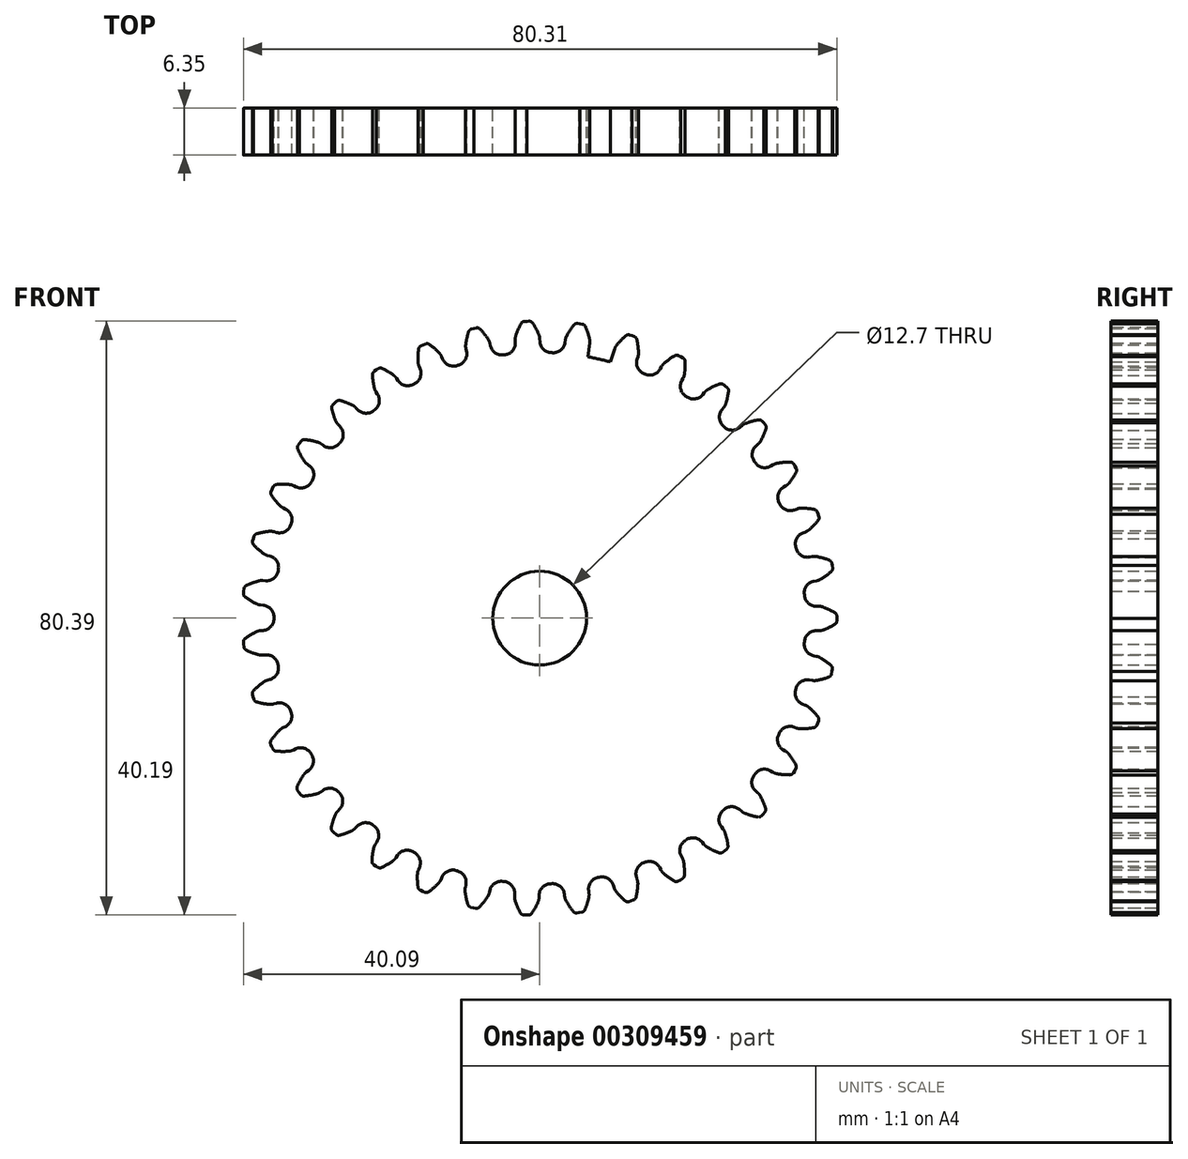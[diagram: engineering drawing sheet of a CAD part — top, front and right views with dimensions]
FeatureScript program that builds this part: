
annotation { "Feature Type Name" : "Feature", "Feature Type Description" : "" }
export const myFeature = defineFeature(function(context is Context, id is Id, definition is map)
    precondition{}
    {
        {
            var Q0;
            Q0=qCreatedBy(makeId("Front.planeOp"),FACE);
            var sketch = newSketch(context, id + "F0", { "sketchPlane" : qUnion([Q0])});
            skCircle(sketch, "E0", {"center": v(0, 0) * mm, "radius": 35.98 * mm});
            skArc(sketch, "E1.trimOffspring", {"start": v(-0.11, 38.38) * mm, "mid": v(-0.5, 39.2) * mm, "end": v(-0.97, 39.97) * mm});
            skLineSegment(sketch, "E2", {"start": v(0.01, 37.83) * mm, "end": v(0.1, 35.98) * mm});
            skLineSegment(sketch, "E3", {"start": v(-1.4, 40.2) * mm, "end": v(-1.75, 40.18) * mm});
            skLineSegment(sketch, "E4.MirrorCS", {"start": v(-2.1, 40.16) * mm, "end": v(-1.75, 40.18) * mm});
            skArc(sketch, "E5.MirrorCS", {"start": v(-3.23, 38.24) * mm, "mid": v(-2.92, 39.09) * mm, "end": v(-2.52, 39.9) * mm});
            skLineSegment(sketch, "E6.MirrorCS", {"start": v(-3.3, 37.68) * mm, "end": v(-3.23, 35.83) * mm});
            skPoint(sketch, "E7.visualSharp", {"position": v(-3.32, 37.96) * mm});
            skArc(sketch, "E7.filletArc", {"start": v(-3.23, 38.24) * mm, "mid": v(-3.3, 37.97) * mm, "end": v(-3.3, 37.68) * mm});
            skPoint(sketch, "E8.visualSharp", {"position": v(0, 38.1) * mm});
            skArc(sketch, "E8.filletArc", {"start": v(0.01, 37.83) * mm, "mid": v(-0.03, 38.1) * mm, "end": v(-0.11, 38.38) * mm});
            skPoint(sketch, "E9.visualSharp", {"position": v(-1.13, 40.2) * mm});
            skArc(sketch, "E9.filletArc", {"start": v(-0.97, 39.97) * mm, "mid": v(-1.16, 40.14) * mm, "end": v(-1.4, 40.2) * mm});
            skPoint(sketch, "E10.visualSharp", {"position": v(-2.38, 40.15) * mm});
            skArc(sketch, "E10.filletArc", {"start": v(-2.1, 40.16) * mm, "mid": v(-2.34, 40.09) * mm, "end": v(-2.52, 39.9) * mm});
            skSolve(sketch);
        }
        {
            var Q0;
            Q0=qCreatedBy(makeId("Front.planeOp"),FACE);
            cPlane(context, id + "F1", {"entities" : qUnion([Q0]), "cplaneType" : CPlaneType.OFFSET, "offset" : 6.35 * mm, "width" : 152.4 * mm, "height" : 152.4 * mm});
        }
        {
            var Q0;
            Q0=qCreatedBy(id+"F1.planeOp",FACE);
            var sketch = newSketch(context, id + "F2", { "sketchPlane" : qUnion([Q0])});
            skArc(sketch, "E11.0.0", {"start": v(-3.23, 35.83) * mm, "mid": v(1.57, -35.94) * mm, "end": v(0.1, 35.98) * mm});
            skArc(sketch, "E11.0.1", {"start": v(0.1, 35.98) * mm, "mid": v(-1.57, 35.94) * mm, "end": v(-3.23, 35.83) * mm});
            skArc(sketch, "E12.0.0", {"start": v(-2.52, 39.9) * mm, "mid": v(-2.92, 39.09) * mm, "end": v(-3.23, 38.24) * mm});
            skArc(sketch, "E12.0.1", {"start": v(-3.23, 38.24) * mm, "mid": v(-3.3, 37.97) * mm, "end": v(-3.3, 37.68) * mm});
            skLineSegment(sketch, "E12.0.2", {"start": v(-3.3, 37.68) * mm, "end": v(-3.23, 35.83) * mm});
            skArc(sketch, "E12.0.3", {"start": v(-3.23, 35.83) * mm, "mid": v(-1.57, 35.94) * mm, "end": v(0.1, 35.98) * mm});
            skLineSegment(sketch, "E12.0.4", {"start": v(0.1, 35.98) * mm, "end": v(0.01, 37.83) * mm});
            skArc(sketch, "E12.0.5", {"start": v(0.01, 37.83) * mm, "mid": v(-0.03, 38.1) * mm, "end": v(-0.11, 38.38) * mm});
            skArc(sketch, "E12.0.6", {"start": v(-0.11, 38.38) * mm, "mid": v(-0.5, 39.2) * mm, "end": v(-0.97, 39.97) * mm});
            skArc(sketch, "E12.0.7", {"start": v(-0.97, 39.97) * mm, "mid": v(-1.16, 40.14) * mm, "end": v(-1.4, 40.2) * mm});
            skLineSegment(sketch, "E12.0.8", {"start": v(-1.4, 40.2) * mm, "end": v(-1.75, 40.18) * mm});
            skLineSegment(sketch, "E12.0.9", {"start": v(-1.75, 40.18) * mm, "end": v(-2.1, 40.16) * mm});
            skArc(sketch, "E12.0.10", {"start": v(-2.1, 40.16) * mm, "mid": v(-2.34, 40.09) * mm, "end": v(-2.52, 39.9) * mm});
            skSolve(sketch);
        }
        {
            var Q0;
            Q0=makeQuery(id+"F2.imprint","IMPRINT",FACE,{"disambiguationData":[TD([[makeQuery(id+"F2.imprint","IMPRINT",EDGE,{"derivedFrom":sQuery(id+"F2.wireOp",EDGE,"E12.0.0")}),1.0]])]});
            var Q1;
            Q1=makeQuery(id+"F0.imprint","IMPRINT",FACE,{"disambiguationData":[TD([[makeQuery(id+"F0.imprint","IMPRINT",EDGE,{"derivedFrom":sQuery(id+"F0.wireOp",EDGE,"E1.trimOffspring")}),1.0]])]});
            loft(context, id + "F3", {"sheetProfilesArray" : [{ "sheetProfileEntities" : qUnion([Q0]) }, { "sheetProfileEntities" : qUnion([Q1]) }]});
        }
        {
            var Q0;
            Q0=qCreatedBy(makeId("Front.planeOp"),FACE);
            var sketch = newSketch(context, id + "F4", { "sketchPlane" : qUnion([Q0])});
            skCircle(sketch, "E13", {"center": v(0, 0) * mm, "radius": 35.98 * mm});
            skSolve(sketch);
        }
        {
            var Q0;
            Q0=makeQuery(id+"F4.imprint","IMPRINT",FACE,{"disambiguationData":[TD([[makeQuery(id+"F4.imprint","IMPRINT",EDGE,{"derivedFrom":sQuery(id+"F4.wireOp",EDGE,"E13")}),1.0]])]});
            var Q1;
            Q1=makeQuery(id+"F3.opLoft","CAP_FACE",FACE,{"disambiguationData":[OSD([makeQuery(id+"F2.imprint","IMPRINT",FACE,{"disambiguationData":[TD([[makeQuery(id+"F2.imprint","IMPRINT",EDGE,{"derivedFrom":sQuery(id+"F2.wireOp",EDGE,"E12.0.0")}),1.0]])]})])],"isStart":true});
            extrude(context, id + "F5", {"entities" : qUnion([Q0]), "endBound" : BoundingType.UP_TO_SURFACE, "endBoundEntityFace" : qUnion([Q1]), "depth" : 25.4 * mm});
        }
        {
            var Q0;
            Q0=makeQuery(id+"F3.opLoft","SWEPT_BODY",BODY,{"disambiguationData":[OSD([makeQuery(id+"F0.imprint","IMPRINT",FACE,{"disambiguationData":[TD([[makeQuery(id+"F0.imprint","IMPRINT",EDGE,{"derivedFrom":sQuery(id+"F0.wireOp",EDGE,"E1.trimOffspring")}),1.0]])]}),makeQuery(id+"F2.imprint","IMPRINT",FACE,{"disambiguationData":[TD([[makeQuery(id+"F2.imprint","IMPRINT",EDGE,{"derivedFrom":sQuery(id+"F2.wireOp",EDGE,"E12.0.0")}),1.0]])]})])]});
            var Q1;
            Q1=makeQuery(id+"F5.opExtrude","SWEPT_FACE",FACE,{"disambiguationData":[OSD([sQuery(id+"F4.wireOp",EDGE,"E13")])]});
            circularPattern(context, id + "F6", {"entities" : qUnion([Q0]), "axis" : qUnion([Q1]), "angle" : 360 * degree, "instanceCount" : 35, "equalSpace" : true});
        }
        {
            var Q0;
            Q0=makeQuery(id+"F6.opPattern","COPY",BODY,{"derivedFrom":makeQuery(id+"F3.opLoft","SWEPT_BODY",BODY,{"disambiguationData":[OSD([makeQuery(id+"F0.imprint","IMPRINT",FACE,{"disambiguationData":[TD([[makeQuery(id+"F0.imprint","IMPRINT",EDGE,{"derivedFrom":sQuery(id+"F0.wireOp",EDGE,"E1.trimOffspring")}),1.0]])]}),makeQuery(id+"F2.imprint","IMPRINT",FACE,{"disambiguationData":[TD([[makeQuery(id+"F2.imprint","IMPRINT",EDGE,{"derivedFrom":sQuery(id+"F2.wireOp",EDGE,"E12.0.0")}),1.0]])]})])]}),"instanceName":"1"});
            var Q1;
            Q1=makeQuery(id+"F5.opExtrude","SWEPT_BODY",BODY,{"disambiguationData":[OSD([sQuery(id+"F4.wireOp",EDGE,"E13")])]});
            var Q2;
            Q2=makeQuery(id+"F3.opLoft","SWEPT_BODY",BODY,{"disambiguationData":[OSD([makeQuery(id+"F0.imprint","IMPRINT",FACE,{"disambiguationData":[TD([[makeQuery(id+"F0.imprint","IMPRINT",EDGE,{"derivedFrom":sQuery(id+"F0.wireOp",EDGE,"E1.trimOffspring")}),1.0]])]}),makeQuery(id+"F2.imprint","IMPRINT",FACE,{"disambiguationData":[TD([[makeQuery(id+"F2.imprint","IMPRINT",EDGE,{"derivedFrom":sQuery(id+"F2.wireOp",EDGE,"E12.0.0")}),1.0]])]})])]});
            var Q3;
            Q3=makeQuery(id+"F6.opPattern","COPY",BODY,{"derivedFrom":makeQuery(id+"F3.opLoft","SWEPT_BODY",BODY,{"disambiguationData":[OSD([makeQuery(id+"F0.imprint","IMPRINT",FACE,{"disambiguationData":[TD([[makeQuery(id+"F0.imprint","IMPRINT",EDGE,{"derivedFrom":sQuery(id+"F0.wireOp",EDGE,"E1.trimOffspring")}),1.0]])]}),makeQuery(id+"F2.imprint","IMPRINT",FACE,{"disambiguationData":[TD([[makeQuery(id+"F2.imprint","IMPRINT",EDGE,{"derivedFrom":sQuery(id+"F2.wireOp",EDGE,"E12.0.0")}),1.0]])]})])]}),"instanceName":"34"});
            var Q4;
            Q4=makeQuery(id+"F6.opPattern","COPY",BODY,{"derivedFrom":makeQuery(id+"F3.opLoft","SWEPT_BODY",BODY,{"disambiguationData":[OSD([makeQuery(id+"F0.imprint","IMPRINT",FACE,{"disambiguationData":[TD([[makeQuery(id+"F0.imprint","IMPRINT",EDGE,{"derivedFrom":sQuery(id+"F0.wireOp",EDGE,"E1.trimOffspring")}),1.0]])]}),makeQuery(id+"F2.imprint","IMPRINT",FACE,{"disambiguationData":[TD([[makeQuery(id+"F2.imprint","IMPRINT",EDGE,{"derivedFrom":sQuery(id+"F2.wireOp",EDGE,"E12.0.0")}),1.0]])]})])]}),"instanceName":"33"});
            var Q5;
            Q5=makeQuery(id+"F6.opPattern","COPY",BODY,{"derivedFrom":makeQuery(id+"F3.opLoft","SWEPT_BODY",BODY,{"disambiguationData":[OSD([makeQuery(id+"F0.imprint","IMPRINT",FACE,{"disambiguationData":[TD([[makeQuery(id+"F0.imprint","IMPRINT",EDGE,{"derivedFrom":sQuery(id+"F0.wireOp",EDGE,"E1.trimOffspring")}),1.0]])]}),makeQuery(id+"F2.imprint","IMPRINT",FACE,{"disambiguationData":[TD([[makeQuery(id+"F2.imprint","IMPRINT",EDGE,{"derivedFrom":sQuery(id+"F2.wireOp",EDGE,"E12.0.0")}),1.0]])]})])]}),"instanceName":"32"});
            var Q6;
            Q6=makeQuery(id+"F6.opPattern","COPY",BODY,{"derivedFrom":makeQuery(id+"F3.opLoft","SWEPT_BODY",BODY,{"disambiguationData":[OSD([makeQuery(id+"F0.imprint","IMPRINT",FACE,{"disambiguationData":[TD([[makeQuery(id+"F0.imprint","IMPRINT",EDGE,{"derivedFrom":sQuery(id+"F0.wireOp",EDGE,"E1.trimOffspring")}),1.0]])]}),makeQuery(id+"F2.imprint","IMPRINT",FACE,{"disambiguationData":[TD([[makeQuery(id+"F2.imprint","IMPRINT",EDGE,{"derivedFrom":sQuery(id+"F2.wireOp",EDGE,"E12.0.0")}),1.0]])]})])]}),"instanceName":"31"});
            var Q7;
            Q7=makeQuery(id+"F6.opPattern","COPY",BODY,{"derivedFrom":makeQuery(id+"F3.opLoft","SWEPT_BODY",BODY,{"disambiguationData":[OSD([makeQuery(id+"F0.imprint","IMPRINT",FACE,{"disambiguationData":[TD([[makeQuery(id+"F0.imprint","IMPRINT",EDGE,{"derivedFrom":sQuery(id+"F0.wireOp",EDGE,"E1.trimOffspring")}),1.0]])]}),makeQuery(id+"F2.imprint","IMPRINT",FACE,{"disambiguationData":[TD([[makeQuery(id+"F2.imprint","IMPRINT",EDGE,{"derivedFrom":sQuery(id+"F2.wireOp",EDGE,"E12.0.0")}),1.0]])]})])]}),"instanceName":"30"});
            var Q8;
            Q8=makeQuery(id+"F6.opPattern","COPY",BODY,{"derivedFrom":makeQuery(id+"F3.opLoft","SWEPT_BODY",BODY,{"disambiguationData":[OSD([makeQuery(id+"F0.imprint","IMPRINT",FACE,{"disambiguationData":[TD([[makeQuery(id+"F0.imprint","IMPRINT",EDGE,{"derivedFrom":sQuery(id+"F0.wireOp",EDGE,"E1.trimOffspring")}),1.0]])]}),makeQuery(id+"F2.imprint","IMPRINT",FACE,{"disambiguationData":[TD([[makeQuery(id+"F2.imprint","IMPRINT",EDGE,{"derivedFrom":sQuery(id+"F2.wireOp",EDGE,"E12.0.0")}),1.0]])]})])]}),"instanceName":"29"});
            var Q9;
            Q9=makeQuery(id+"F6.opPattern","COPY",BODY,{"derivedFrom":makeQuery(id+"F3.opLoft","SWEPT_BODY",BODY,{"disambiguationData":[OSD([makeQuery(id+"F0.imprint","IMPRINT",FACE,{"disambiguationData":[TD([[makeQuery(id+"F0.imprint","IMPRINT",EDGE,{"derivedFrom":sQuery(id+"F0.wireOp",EDGE,"E1.trimOffspring")}),1.0]])]}),makeQuery(id+"F2.imprint","IMPRINT",FACE,{"disambiguationData":[TD([[makeQuery(id+"F2.imprint","IMPRINT",EDGE,{"derivedFrom":sQuery(id+"F2.wireOp",EDGE,"E12.0.0")}),1.0]])]})])]}),"instanceName":"2"});
            var Q10;
            Q10=makeQuery(id+"F6.opPattern","COPY",BODY,{"derivedFrom":makeQuery(id+"F3.opLoft","SWEPT_BODY",BODY,{"disambiguationData":[OSD([makeQuery(id+"F0.imprint","IMPRINT",FACE,{"disambiguationData":[TD([[makeQuery(id+"F0.imprint","IMPRINT",EDGE,{"derivedFrom":sQuery(id+"F0.wireOp",EDGE,"E1.trimOffspring")}),1.0]])]}),makeQuery(id+"F2.imprint","IMPRINT",FACE,{"disambiguationData":[TD([[makeQuery(id+"F2.imprint","IMPRINT",EDGE,{"derivedFrom":sQuery(id+"F2.wireOp",EDGE,"E12.0.0")}),1.0]])]})])]}),"instanceName":"3"});
            var Q11;
            Q11=makeQuery(id+"F6.opPattern","COPY",BODY,{"derivedFrom":makeQuery(id+"F3.opLoft","SWEPT_BODY",BODY,{"disambiguationData":[OSD([makeQuery(id+"F0.imprint","IMPRINT",FACE,{"disambiguationData":[TD([[makeQuery(id+"F0.imprint","IMPRINT",EDGE,{"derivedFrom":sQuery(id+"F0.wireOp",EDGE,"E1.trimOffspring")}),1.0]])]}),makeQuery(id+"F2.imprint","IMPRINT",FACE,{"disambiguationData":[TD([[makeQuery(id+"F2.imprint","IMPRINT",EDGE,{"derivedFrom":sQuery(id+"F2.wireOp",EDGE,"E12.0.0")}),1.0]])]})])]}),"instanceName":"4"});
            var Q12;
            Q12=makeQuery(id+"F6.opPattern","COPY",BODY,{"derivedFrom":makeQuery(id+"F3.opLoft","SWEPT_BODY",BODY,{"disambiguationData":[OSD([makeQuery(id+"F0.imprint","IMPRINT",FACE,{"disambiguationData":[TD([[makeQuery(id+"F0.imprint","IMPRINT",EDGE,{"derivedFrom":sQuery(id+"F0.wireOp",EDGE,"E1.trimOffspring")}),1.0]])]}),makeQuery(id+"F2.imprint","IMPRINT",FACE,{"disambiguationData":[TD([[makeQuery(id+"F2.imprint","IMPRINT",EDGE,{"derivedFrom":sQuery(id+"F2.wireOp",EDGE,"E12.0.0")}),1.0]])]})])]}),"instanceName":"5"});
            var Q13;
            Q13=makeQuery(id+"F6.opPattern","COPY",BODY,{"derivedFrom":makeQuery(id+"F3.opLoft","SWEPT_BODY",BODY,{"disambiguationData":[OSD([makeQuery(id+"F0.imprint","IMPRINT",FACE,{"disambiguationData":[TD([[makeQuery(id+"F0.imprint","IMPRINT",EDGE,{"derivedFrom":sQuery(id+"F0.wireOp",EDGE,"E1.trimOffspring")}),1.0]])]}),makeQuery(id+"F2.imprint","IMPRINT",FACE,{"disambiguationData":[TD([[makeQuery(id+"F2.imprint","IMPRINT",EDGE,{"derivedFrom":sQuery(id+"F2.wireOp",EDGE,"E12.0.0")}),1.0]])]})])]}),"instanceName":"6"});
            var Q14;
            Q14=makeQuery(id+"F6.opPattern","COPY",BODY,{"derivedFrom":makeQuery(id+"F3.opLoft","SWEPT_BODY",BODY,{"disambiguationData":[OSD([makeQuery(id+"F0.imprint","IMPRINT",FACE,{"disambiguationData":[TD([[makeQuery(id+"F0.imprint","IMPRINT",EDGE,{"derivedFrom":sQuery(id+"F0.wireOp",EDGE,"E1.trimOffspring")}),1.0]])]}),makeQuery(id+"F2.imprint","IMPRINT",FACE,{"disambiguationData":[TD([[makeQuery(id+"F2.imprint","IMPRINT",EDGE,{"derivedFrom":sQuery(id+"F2.wireOp",EDGE,"E12.0.0")}),1.0]])]})])]}),"instanceName":"7"});
            var Q15;
            Q15=makeQuery(id+"F6.opPattern","COPY",BODY,{"derivedFrom":makeQuery(id+"F3.opLoft","SWEPT_BODY",BODY,{"disambiguationData":[OSD([makeQuery(id+"F0.imprint","IMPRINT",FACE,{"disambiguationData":[TD([[makeQuery(id+"F0.imprint","IMPRINT",EDGE,{"derivedFrom":sQuery(id+"F0.wireOp",EDGE,"E1.trimOffspring")}),1.0]])]}),makeQuery(id+"F2.imprint","IMPRINT",FACE,{"disambiguationData":[TD([[makeQuery(id+"F2.imprint","IMPRINT",EDGE,{"derivedFrom":sQuery(id+"F2.wireOp",EDGE,"E12.0.0")}),1.0]])]})])]}),"instanceName":"8"});
            var Q16;
            Q16=makeQuery(id+"F6.opPattern","COPY",BODY,{"derivedFrom":makeQuery(id+"F3.opLoft","SWEPT_BODY",BODY,{"disambiguationData":[OSD([makeQuery(id+"F0.imprint","IMPRINT",FACE,{"disambiguationData":[TD([[makeQuery(id+"F0.imprint","IMPRINT",EDGE,{"derivedFrom":sQuery(id+"F0.wireOp",EDGE,"E1.trimOffspring")}),1.0]])]}),makeQuery(id+"F2.imprint","IMPRINT",FACE,{"disambiguationData":[TD([[makeQuery(id+"F2.imprint","IMPRINT",EDGE,{"derivedFrom":sQuery(id+"F2.wireOp",EDGE,"E12.0.0")}),1.0]])]})])]}),"instanceName":"9"});
            var Q17;
            Q17=makeQuery(id+"F6.opPattern","COPY",BODY,{"derivedFrom":makeQuery(id+"F3.opLoft","SWEPT_BODY",BODY,{"disambiguationData":[OSD([makeQuery(id+"F0.imprint","IMPRINT",FACE,{"disambiguationData":[TD([[makeQuery(id+"F0.imprint","IMPRINT",EDGE,{"derivedFrom":sQuery(id+"F0.wireOp",EDGE,"E1.trimOffspring")}),1.0]])]}),makeQuery(id+"F2.imprint","IMPRINT",FACE,{"disambiguationData":[TD([[makeQuery(id+"F2.imprint","IMPRINT",EDGE,{"derivedFrom":sQuery(id+"F2.wireOp",EDGE,"E12.0.0")}),1.0]])]})])]}),"instanceName":"10"});
            var Q18;
            Q18=makeQuery(id+"F6.opPattern","COPY",BODY,{"derivedFrom":makeQuery(id+"F3.opLoft","SWEPT_BODY",BODY,{"disambiguationData":[OSD([makeQuery(id+"F0.imprint","IMPRINT",FACE,{"disambiguationData":[TD([[makeQuery(id+"F0.imprint","IMPRINT",EDGE,{"derivedFrom":sQuery(id+"F0.wireOp",EDGE,"E1.trimOffspring")}),1.0]])]}),makeQuery(id+"F2.imprint","IMPRINT",FACE,{"disambiguationData":[TD([[makeQuery(id+"F2.imprint","IMPRINT",EDGE,{"derivedFrom":sQuery(id+"F2.wireOp",EDGE,"E12.0.0")}),1.0]])]})])]}),"instanceName":"27"});
            var Q19;
            Q19=makeQuery(id+"F6.opPattern","COPY",BODY,{"derivedFrom":makeQuery(id+"F3.opLoft","SWEPT_BODY",BODY,{"disambiguationData":[OSD([makeQuery(id+"F0.imprint","IMPRINT",FACE,{"disambiguationData":[TD([[makeQuery(id+"F0.imprint","IMPRINT",EDGE,{"derivedFrom":sQuery(id+"F0.wireOp",EDGE,"E1.trimOffspring")}),1.0]])]}),makeQuery(id+"F2.imprint","IMPRINT",FACE,{"disambiguationData":[TD([[makeQuery(id+"F2.imprint","IMPRINT",EDGE,{"derivedFrom":sQuery(id+"F2.wireOp",EDGE,"E12.0.0")}),1.0]])]})])]}),"instanceName":"28"});
            var Q20;
            Q20=makeQuery(id+"F6.opPattern","COPY",BODY,{"derivedFrom":makeQuery(id+"F3.opLoft","SWEPT_BODY",BODY,{"disambiguationData":[OSD([makeQuery(id+"F0.imprint","IMPRINT",FACE,{"disambiguationData":[TD([[makeQuery(id+"F0.imprint","IMPRINT",EDGE,{"derivedFrom":sQuery(id+"F0.wireOp",EDGE,"E1.trimOffspring")}),1.0]])]}),makeQuery(id+"F2.imprint","IMPRINT",FACE,{"disambiguationData":[TD([[makeQuery(id+"F2.imprint","IMPRINT",EDGE,{"derivedFrom":sQuery(id+"F2.wireOp",EDGE,"E12.0.0")}),1.0]])]})])]}),"instanceName":"26"});
            var Q21;
            Q21=makeQuery(id+"F6.opPattern","COPY",BODY,{"derivedFrom":makeQuery(id+"F3.opLoft","SWEPT_BODY",BODY,{"disambiguationData":[OSD([makeQuery(id+"F0.imprint","IMPRINT",FACE,{"disambiguationData":[TD([[makeQuery(id+"F0.imprint","IMPRINT",EDGE,{"derivedFrom":sQuery(id+"F0.wireOp",EDGE,"E1.trimOffspring")}),1.0]])]}),makeQuery(id+"F2.imprint","IMPRINT",FACE,{"disambiguationData":[TD([[makeQuery(id+"F2.imprint","IMPRINT",EDGE,{"derivedFrom":sQuery(id+"F2.wireOp",EDGE,"E12.0.0")}),1.0]])]})])]}),"instanceName":"25"});
            var Q22;
            Q22=makeQuery(id+"F6.opPattern","COPY",BODY,{"derivedFrom":makeQuery(id+"F3.opLoft","SWEPT_BODY",BODY,{"disambiguationData":[OSD([makeQuery(id+"F0.imprint","IMPRINT",FACE,{"disambiguationData":[TD([[makeQuery(id+"F0.imprint","IMPRINT",EDGE,{"derivedFrom":sQuery(id+"F0.wireOp",EDGE,"E1.trimOffspring")}),1.0]])]}),makeQuery(id+"F2.imprint","IMPRINT",FACE,{"disambiguationData":[TD([[makeQuery(id+"F2.imprint","IMPRINT",EDGE,{"derivedFrom":sQuery(id+"F2.wireOp",EDGE,"E12.0.0")}),1.0]])]})])]}),"instanceName":"24"});
            var Q23;
            Q23=makeQuery(id+"F6.opPattern","COPY",BODY,{"derivedFrom":makeQuery(id+"F3.opLoft","SWEPT_BODY",BODY,{"disambiguationData":[OSD([makeQuery(id+"F0.imprint","IMPRINT",FACE,{"disambiguationData":[TD([[makeQuery(id+"F0.imprint","IMPRINT",EDGE,{"derivedFrom":sQuery(id+"F0.wireOp",EDGE,"E1.trimOffspring")}),1.0]])]}),makeQuery(id+"F2.imprint","IMPRINT",FACE,{"disambiguationData":[TD([[makeQuery(id+"F2.imprint","IMPRINT",EDGE,{"derivedFrom":sQuery(id+"F2.wireOp",EDGE,"E12.0.0")}),1.0]])]})])]}),"instanceName":"23"});
            var Q24;
            Q24=makeQuery(id+"F6.opPattern","COPY",BODY,{"derivedFrom":makeQuery(id+"F3.opLoft","SWEPT_BODY",BODY,{"disambiguationData":[OSD([makeQuery(id+"F0.imprint","IMPRINT",FACE,{"disambiguationData":[TD([[makeQuery(id+"F0.imprint","IMPRINT",EDGE,{"derivedFrom":sQuery(id+"F0.wireOp",EDGE,"E1.trimOffspring")}),1.0]])]}),makeQuery(id+"F2.imprint","IMPRINT",FACE,{"disambiguationData":[TD([[makeQuery(id+"F2.imprint","IMPRINT",EDGE,{"derivedFrom":sQuery(id+"F2.wireOp",EDGE,"E12.0.0")}),1.0]])]})])]}),"instanceName":"22"});
            var Q25;
            Q25=makeQuery(id+"F6.opPattern","COPY",BODY,{"derivedFrom":makeQuery(id+"F3.opLoft","SWEPT_BODY",BODY,{"disambiguationData":[OSD([makeQuery(id+"F0.imprint","IMPRINT",FACE,{"disambiguationData":[TD([[makeQuery(id+"F0.imprint","IMPRINT",EDGE,{"derivedFrom":sQuery(id+"F0.wireOp",EDGE,"E1.trimOffspring")}),1.0]])]}),makeQuery(id+"F2.imprint","IMPRINT",FACE,{"disambiguationData":[TD([[makeQuery(id+"F2.imprint","IMPRINT",EDGE,{"derivedFrom":sQuery(id+"F2.wireOp",EDGE,"E12.0.0")}),1.0]])]})])]}),"instanceName":"21"});
            var Q26;
            Q26=makeQuery(id+"F6.opPattern","COPY",BODY,{"derivedFrom":makeQuery(id+"F3.opLoft","SWEPT_BODY",BODY,{"disambiguationData":[OSD([makeQuery(id+"F0.imprint","IMPRINT",FACE,{"disambiguationData":[TD([[makeQuery(id+"F0.imprint","IMPRINT",EDGE,{"derivedFrom":sQuery(id+"F0.wireOp",EDGE,"E1.trimOffspring")}),1.0]])]}),makeQuery(id+"F2.imprint","IMPRINT",FACE,{"disambiguationData":[TD([[makeQuery(id+"F2.imprint","IMPRINT",EDGE,{"derivedFrom":sQuery(id+"F2.wireOp",EDGE,"E12.0.0")}),1.0]])]})])]}),"instanceName":"20"});
            var Q27;
            Q27=makeQuery(id+"F6.opPattern","COPY",BODY,{"derivedFrom":makeQuery(id+"F3.opLoft","SWEPT_BODY",BODY,{"disambiguationData":[OSD([makeQuery(id+"F0.imprint","IMPRINT",FACE,{"disambiguationData":[TD([[makeQuery(id+"F0.imprint","IMPRINT",EDGE,{"derivedFrom":sQuery(id+"F0.wireOp",EDGE,"E1.trimOffspring")}),1.0]])]}),makeQuery(id+"F2.imprint","IMPRINT",FACE,{"disambiguationData":[TD([[makeQuery(id+"F2.imprint","IMPRINT",EDGE,{"derivedFrom":sQuery(id+"F2.wireOp",EDGE,"E12.0.0")}),1.0]])]})])]}),"instanceName":"19"});
            var Q28;
            Q28=makeQuery(id+"F6.opPattern","COPY",BODY,{"derivedFrom":makeQuery(id+"F3.opLoft","SWEPT_BODY",BODY,{"disambiguationData":[OSD([makeQuery(id+"F0.imprint","IMPRINT",FACE,{"disambiguationData":[TD([[makeQuery(id+"F0.imprint","IMPRINT",EDGE,{"derivedFrom":sQuery(id+"F0.wireOp",EDGE,"E1.trimOffspring")}),1.0]])]}),makeQuery(id+"F2.imprint","IMPRINT",FACE,{"disambiguationData":[TD([[makeQuery(id+"F2.imprint","IMPRINT",EDGE,{"derivedFrom":sQuery(id+"F2.wireOp",EDGE,"E12.0.0")}),1.0]])]})])]}),"instanceName":"18"});
            var Q29;
            Q29=makeQuery(id+"F6.opPattern","COPY",BODY,{"derivedFrom":makeQuery(id+"F3.opLoft","SWEPT_BODY",BODY,{"disambiguationData":[OSD([makeQuery(id+"F0.imprint","IMPRINT",FACE,{"disambiguationData":[TD([[makeQuery(id+"F0.imprint","IMPRINT",EDGE,{"derivedFrom":sQuery(id+"F0.wireOp",EDGE,"E1.trimOffspring")}),1.0]])]}),makeQuery(id+"F2.imprint","IMPRINT",FACE,{"disambiguationData":[TD([[makeQuery(id+"F2.imprint","IMPRINT",EDGE,{"derivedFrom":sQuery(id+"F2.wireOp",EDGE,"E12.0.0")}),1.0]])]})])]}),"instanceName":"17"});
            var Q30;
            Q30=makeQuery(id+"F6.opPattern","COPY",BODY,{"derivedFrom":makeQuery(id+"F3.opLoft","SWEPT_BODY",BODY,{"disambiguationData":[OSD([makeQuery(id+"F0.imprint","IMPRINT",FACE,{"disambiguationData":[TD([[makeQuery(id+"F0.imprint","IMPRINT",EDGE,{"derivedFrom":sQuery(id+"F0.wireOp",EDGE,"E1.trimOffspring")}),1.0]])]}),makeQuery(id+"F2.imprint","IMPRINT",FACE,{"disambiguationData":[TD([[makeQuery(id+"F2.imprint","IMPRINT",EDGE,{"derivedFrom":sQuery(id+"F2.wireOp",EDGE,"E12.0.0")}),1.0]])]})])]}),"instanceName":"16"});
            var Q31;
            Q31=makeQuery(id+"F6.opPattern","COPY",BODY,{"derivedFrom":makeQuery(id+"F3.opLoft","SWEPT_BODY",BODY,{"disambiguationData":[OSD([makeQuery(id+"F0.imprint","IMPRINT",FACE,{"disambiguationData":[TD([[makeQuery(id+"F0.imprint","IMPRINT",EDGE,{"derivedFrom":sQuery(id+"F0.wireOp",EDGE,"E1.trimOffspring")}),1.0]])]}),makeQuery(id+"F2.imprint","IMPRINT",FACE,{"disambiguationData":[TD([[makeQuery(id+"F2.imprint","IMPRINT",EDGE,{"derivedFrom":sQuery(id+"F2.wireOp",EDGE,"E12.0.0")}),1.0]])]})])]}),"instanceName":"15"});
            var Q32;
            Q32=makeQuery(id+"F6.opPattern","COPY",BODY,{"derivedFrom":makeQuery(id+"F3.opLoft","SWEPT_BODY",BODY,{"disambiguationData":[OSD([makeQuery(id+"F0.imprint","IMPRINT",FACE,{"disambiguationData":[TD([[makeQuery(id+"F0.imprint","IMPRINT",EDGE,{"derivedFrom":sQuery(id+"F0.wireOp",EDGE,"E1.trimOffspring")}),1.0]])]}),makeQuery(id+"F2.imprint","IMPRINT",FACE,{"disambiguationData":[TD([[makeQuery(id+"F2.imprint","IMPRINT",EDGE,{"derivedFrom":sQuery(id+"F2.wireOp",EDGE,"E12.0.0")}),1.0]])]})])]}),"instanceName":"14"});
            var Q33;
            Q33=makeQuery(id+"F6.opPattern","COPY",BODY,{"derivedFrom":makeQuery(id+"F3.opLoft","SWEPT_BODY",BODY,{"disambiguationData":[OSD([makeQuery(id+"F0.imprint","IMPRINT",FACE,{"disambiguationData":[TD([[makeQuery(id+"F0.imprint","IMPRINT",EDGE,{"derivedFrom":sQuery(id+"F0.wireOp",EDGE,"E1.trimOffspring")}),1.0]])]}),makeQuery(id+"F2.imprint","IMPRINT",FACE,{"disambiguationData":[TD([[makeQuery(id+"F2.imprint","IMPRINT",EDGE,{"derivedFrom":sQuery(id+"F2.wireOp",EDGE,"E12.0.0")}),1.0]])]})])]}),"instanceName":"13"});
            var Q34;
            Q34=makeQuery(id+"F6.opPattern","COPY",BODY,{"derivedFrom":makeQuery(id+"F3.opLoft","SWEPT_BODY",BODY,{"disambiguationData":[OSD([makeQuery(id+"F0.imprint","IMPRINT",FACE,{"disambiguationData":[TD([[makeQuery(id+"F0.imprint","IMPRINT",EDGE,{"derivedFrom":sQuery(id+"F0.wireOp",EDGE,"E1.trimOffspring")}),1.0]])]}),makeQuery(id+"F2.imprint","IMPRINT",FACE,{"disambiguationData":[TD([[makeQuery(id+"F2.imprint","IMPRINT",EDGE,{"derivedFrom":sQuery(id+"F2.wireOp",EDGE,"E12.0.0")}),1.0]])]})])]}),"instanceName":"12"});
            var Q35;
            Q35=makeQuery(id+"F6.opPattern","COPY",BODY,{"derivedFrom":makeQuery(id+"F3.opLoft","SWEPT_BODY",BODY,{"disambiguationData":[OSD([makeQuery(id+"F0.imprint","IMPRINT",FACE,{"disambiguationData":[TD([[makeQuery(id+"F0.imprint","IMPRINT",EDGE,{"derivedFrom":sQuery(id+"F0.wireOp",EDGE,"E1.trimOffspring")}),1.0]])]}),makeQuery(id+"F2.imprint","IMPRINT",FACE,{"disambiguationData":[TD([[makeQuery(id+"F2.imprint","IMPRINT",EDGE,{"derivedFrom":sQuery(id+"F2.wireOp",EDGE,"E12.0.0")}),1.0]])]})])]}),"instanceName":"11"});
            booleanBodies(context, id + "F7", {"operationType" : BooleanOperationType.UNION, "tools" : qUnion([Q0, Q1, Q2, Q3, Q4, Q5, Q6, Q7, Q8, Q9, Q10, Q11, Q12, Q13, Q14, Q15, Q16, Q17, Q18, Q19, Q20, Q21, Q22, Q23, Q24, Q25, Q26, Q27, Q28, Q29, Q30, Q31, Q32, Q33, Q34, Q35])});
        }
        {
            var Q0;
            Q0=makeQuery(id+"F3.opLoft","SWEPT_EDGE",EDGE,{"disambiguationData":[OSD([sQuery(id+"F0.wireOp",EDGE,"E0"),sQuery(id+"F0.wireOp",EDGE,"E2"),sQuery(id+"F2.wireOp",EDGE,"E11.0.0"),sQuery(id+"F2.wireOp",EDGE,"E12.0.3"),sQuery(id+"F2.wireOp",EDGE,"E12.0.4")])]});
            var Q1;
            Q1=makeQuery(id+"F6.opPattern","COPY",EDGE,{"derivedFrom":makeQuery(id+"F3.opLoft","SWEPT_EDGE",EDGE,{"disambiguationData":[OSD([sQuery(id+"F0.wireOp",EDGE,"E0"),sQuery(id+"F0.wireOp",EDGE,"E2"),sQuery(id+"F2.wireOp",EDGE,"E11.0.0"),sQuery(id+"F2.wireOp",EDGE,"E12.0.3"),sQuery(id+"F2.wireOp",EDGE,"E12.0.4")])]}),"instanceName":"34"});
            var Q2;
            Q2=makeQuery(id+"F6.opPattern","COPY",EDGE,{"derivedFrom":makeQuery(id+"F3.opLoft","SWEPT_EDGE",EDGE,{"disambiguationData":[OSD([sQuery(id+"F0.wireOp",EDGE,"E0"),sQuery(id+"F0.wireOp",EDGE,"E2"),sQuery(id+"F2.wireOp",EDGE,"E11.0.0"),sQuery(id+"F2.wireOp",EDGE,"E12.0.3"),sQuery(id+"F2.wireOp",EDGE,"E12.0.4")])]}),"instanceName":"33"});
            var Q3;
            Q3=makeQuery(id+"F6.opPattern","COPY",EDGE,{"derivedFrom":makeQuery(id+"F3.opLoft","SWEPT_EDGE",EDGE,{"disambiguationData":[OSD([sQuery(id+"F0.wireOp",EDGE,"E0"),sQuery(id+"F0.wireOp",EDGE,"E2"),sQuery(id+"F2.wireOp",EDGE,"E11.0.0"),sQuery(id+"F2.wireOp",EDGE,"E12.0.3"),sQuery(id+"F2.wireOp",EDGE,"E12.0.4")])]}),"instanceName":"32"});
            var Q4;
            Q4=makeQuery(id+"F6.opPattern","COPY",EDGE,{"derivedFrom":makeQuery(id+"F3.opLoft","SWEPT_EDGE",EDGE,{"disambiguationData":[OSD([sQuery(id+"F0.wireOp",EDGE,"E0"),sQuery(id+"F0.wireOp",EDGE,"E2"),sQuery(id+"F2.wireOp",EDGE,"E11.0.0"),sQuery(id+"F2.wireOp",EDGE,"E12.0.3"),sQuery(id+"F2.wireOp",EDGE,"E12.0.4")])]}),"instanceName":"31"});
            var Q5;
            Q5=makeQuery(id+"F3.opLoft","SWEPT_EDGE",EDGE,{"disambiguationData":[OSD([sQuery(id+"F0.wireOp",EDGE,"E0"),sQuery(id+"F0.wireOp",EDGE,"E6.MirrorCS"),sQuery(id+"F2.wireOp",EDGE,"E11.0.0"),sQuery(id+"F2.wireOp",EDGE,"E12.0.2"),sQuery(id+"F2.wireOp",EDGE,"E12.0.3")])]});
            var Q6;
            Q6=makeQuery(id+"F6.opPattern","COPY",EDGE,{"derivedFrom":makeQuery(id+"F3.opLoft","SWEPT_EDGE",EDGE,{"disambiguationData":[OSD([sQuery(id+"F0.wireOp",EDGE,"E0"),sQuery(id+"F0.wireOp",EDGE,"E6.MirrorCS"),sQuery(id+"F2.wireOp",EDGE,"E11.0.0"),sQuery(id+"F2.wireOp",EDGE,"E12.0.2"),sQuery(id+"F2.wireOp",EDGE,"E12.0.3")])]}),"instanceName":"33"});
            var Q7;
            Q7=makeQuery(id+"F6.opPattern","COPY",EDGE,{"derivedFrom":makeQuery(id+"F3.opLoft","SWEPT_EDGE",EDGE,{"disambiguationData":[OSD([sQuery(id+"F0.wireOp",EDGE,"E0"),sQuery(id+"F0.wireOp",EDGE,"E6.MirrorCS"),sQuery(id+"F2.wireOp",EDGE,"E11.0.0"),sQuery(id+"F2.wireOp",EDGE,"E12.0.2"),sQuery(id+"F2.wireOp",EDGE,"E12.0.3")])]}),"instanceName":"34"});
            var Q8;
            Q8=makeQuery(id+"F6.opPattern","COPY",EDGE,{"derivedFrom":makeQuery(id+"F3.opLoft","SWEPT_EDGE",EDGE,{"disambiguationData":[OSD([sQuery(id+"F0.wireOp",EDGE,"E0"),sQuery(id+"F0.wireOp",EDGE,"E6.MirrorCS"),sQuery(id+"F2.wireOp",EDGE,"E11.0.0"),sQuery(id+"F2.wireOp",EDGE,"E12.0.2"),sQuery(id+"F2.wireOp",EDGE,"E12.0.3")])]}),"instanceName":"32"});
            var Q9;
            Q9=makeQuery(id+"F6.opPattern","COPY",EDGE,{"derivedFrom":makeQuery(id+"F3.opLoft","SWEPT_EDGE",EDGE,{"disambiguationData":[OSD([sQuery(id+"F0.wireOp",EDGE,"E0"),sQuery(id+"F0.wireOp",EDGE,"E2"),sQuery(id+"F2.wireOp",EDGE,"E11.0.0"),sQuery(id+"F2.wireOp",EDGE,"E12.0.3"),sQuery(id+"F2.wireOp",EDGE,"E12.0.4")])]}),"instanceName":"30"});
            var Q10;
            Q10=makeQuery(id+"F6.opPattern","COPY",EDGE,{"derivedFrom":makeQuery(id+"F3.opLoft","SWEPT_EDGE",EDGE,{"disambiguationData":[OSD([sQuery(id+"F0.wireOp",EDGE,"E0"),sQuery(id+"F0.wireOp",EDGE,"E6.MirrorCS"),sQuery(id+"F2.wireOp",EDGE,"E11.0.0"),sQuery(id+"F2.wireOp",EDGE,"E12.0.2"),sQuery(id+"F2.wireOp",EDGE,"E12.0.3")])]}),"instanceName":"31"});
            var Q11;
            Q11=makeQuery(id+"F6.opPattern","COPY",EDGE,{"derivedFrom":makeQuery(id+"F3.opLoft","SWEPT_EDGE",EDGE,{"disambiguationData":[OSD([sQuery(id+"F0.wireOp",EDGE,"E0"),sQuery(id+"F0.wireOp",EDGE,"E6.MirrorCS"),sQuery(id+"F2.wireOp",EDGE,"E11.0.0"),sQuery(id+"F2.wireOp",EDGE,"E12.0.2"),sQuery(id+"F2.wireOp",EDGE,"E12.0.3")])]}),"instanceName":"30"});
            var Q12;
            Q12=makeQuery(id+"F6.opPattern","COPY",EDGE,{"derivedFrom":makeQuery(id+"F3.opLoft","SWEPT_EDGE",EDGE,{"disambiguationData":[OSD([sQuery(id+"F0.wireOp",EDGE,"E0"),sQuery(id+"F0.wireOp",EDGE,"E2"),sQuery(id+"F2.wireOp",EDGE,"E11.0.0"),sQuery(id+"F2.wireOp",EDGE,"E12.0.3"),sQuery(id+"F2.wireOp",EDGE,"E12.0.4")])]}),"instanceName":"29"});
            var Q13;
            Q13=makeQuery(id+"F6.opPattern","COPY",EDGE,{"derivedFrom":makeQuery(id+"F3.opLoft","SWEPT_EDGE",EDGE,{"disambiguationData":[OSD([sQuery(id+"F0.wireOp",EDGE,"E0"),sQuery(id+"F0.wireOp",EDGE,"E6.MirrorCS"),sQuery(id+"F2.wireOp",EDGE,"E11.0.0"),sQuery(id+"F2.wireOp",EDGE,"E12.0.2"),sQuery(id+"F2.wireOp",EDGE,"E12.0.3")])]}),"instanceName":"1"});
            var Q14;
            Q14=makeQuery(id+"F6.opPattern","COPY",EDGE,{"derivedFrom":makeQuery(id+"F3.opLoft","SWEPT_EDGE",EDGE,{"disambiguationData":[OSD([sQuery(id+"F0.wireOp",EDGE,"E0"),sQuery(id+"F0.wireOp",EDGE,"E6.MirrorCS"),sQuery(id+"F2.wireOp",EDGE,"E11.0.0"),sQuery(id+"F2.wireOp",EDGE,"E12.0.2"),sQuery(id+"F2.wireOp",EDGE,"E12.0.3")])]}),"instanceName":"2"});
            var Q15;
            Q15=makeQuery(id+"F6.opPattern","COPY",EDGE,{"derivedFrom":makeQuery(id+"F3.opLoft","SWEPT_EDGE",EDGE,{"disambiguationData":[OSD([sQuery(id+"F0.wireOp",EDGE,"E0"),sQuery(id+"F0.wireOp",EDGE,"E6.MirrorCS"),sQuery(id+"F2.wireOp",EDGE,"E11.0.0"),sQuery(id+"F2.wireOp",EDGE,"E12.0.2"),sQuery(id+"F2.wireOp",EDGE,"E12.0.3")])]}),"instanceName":"3"});
            var Q16;
            Q16=makeQuery(id+"F6.opPattern","COPY",EDGE,{"derivedFrom":makeQuery(id+"F3.opLoft","SWEPT_EDGE",EDGE,{"disambiguationData":[OSD([sQuery(id+"F0.wireOp",EDGE,"E0"),sQuery(id+"F0.wireOp",EDGE,"E6.MirrorCS"),sQuery(id+"F2.wireOp",EDGE,"E11.0.0"),sQuery(id+"F2.wireOp",EDGE,"E12.0.2"),sQuery(id+"F2.wireOp",EDGE,"E12.0.3")])]}),"instanceName":"4"});
            var Q17;
            Q17=makeQuery(id+"F6.opPattern","COPY",EDGE,{"derivedFrom":makeQuery(id+"F3.opLoft","SWEPT_EDGE",EDGE,{"disambiguationData":[OSD([sQuery(id+"F0.wireOp",EDGE,"E0"),sQuery(id+"F0.wireOp",EDGE,"E6.MirrorCS"),sQuery(id+"F2.wireOp",EDGE,"E11.0.0"),sQuery(id+"F2.wireOp",EDGE,"E12.0.2"),sQuery(id+"F2.wireOp",EDGE,"E12.0.3")])]}),"instanceName":"5"});
            var Q18;
            Q18=makeQuery(id+"F6.opPattern","COPY",EDGE,{"derivedFrom":makeQuery(id+"F3.opLoft","SWEPT_EDGE",EDGE,{"disambiguationData":[OSD([sQuery(id+"F0.wireOp",EDGE,"E0"),sQuery(id+"F0.wireOp",EDGE,"E6.MirrorCS"),sQuery(id+"F2.wireOp",EDGE,"E11.0.0"),sQuery(id+"F2.wireOp",EDGE,"E12.0.2"),sQuery(id+"F2.wireOp",EDGE,"E12.0.3")])]}),"instanceName":"6"});
            var Q19;
            Q19=makeQuery(id+"F6.opPattern","COPY",EDGE,{"derivedFrom":makeQuery(id+"F3.opLoft","SWEPT_EDGE",EDGE,{"disambiguationData":[OSD([sQuery(id+"F0.wireOp",EDGE,"E0"),sQuery(id+"F0.wireOp",EDGE,"E6.MirrorCS"),sQuery(id+"F2.wireOp",EDGE,"E11.0.0"),sQuery(id+"F2.wireOp",EDGE,"E12.0.2"),sQuery(id+"F2.wireOp",EDGE,"E12.0.3")])]}),"instanceName":"7"});
            var Q20;
            Q20=makeQuery(id+"F6.opPattern","COPY",EDGE,{"derivedFrom":makeQuery(id+"F3.opLoft","SWEPT_EDGE",EDGE,{"disambiguationData":[OSD([sQuery(id+"F0.wireOp",EDGE,"E0"),sQuery(id+"F0.wireOp",EDGE,"E2"),sQuery(id+"F2.wireOp",EDGE,"E11.0.0"),sQuery(id+"F2.wireOp",EDGE,"E12.0.3"),sQuery(id+"F2.wireOp",EDGE,"E12.0.4")])]}),"instanceName":"28"});
            var Q21;
            Q21=makeQuery(id+"F6.opPattern","COPY",EDGE,{"derivedFrom":makeQuery(id+"F3.opLoft","SWEPT_EDGE",EDGE,{"disambiguationData":[OSD([sQuery(id+"F0.wireOp",EDGE,"E0"),sQuery(id+"F0.wireOp",EDGE,"E2"),sQuery(id+"F2.wireOp",EDGE,"E11.0.0"),sQuery(id+"F2.wireOp",EDGE,"E12.0.3"),sQuery(id+"F2.wireOp",EDGE,"E12.0.4")])]}),"instanceName":"27"});
            var Q22;
            Q22=makeQuery(id+"F6.opPattern","COPY",EDGE,{"derivedFrom":makeQuery(id+"F3.opLoft","SWEPT_EDGE",EDGE,{"disambiguationData":[OSD([sQuery(id+"F0.wireOp",EDGE,"E0"),sQuery(id+"F0.wireOp",EDGE,"E2"),sQuery(id+"F2.wireOp",EDGE,"E11.0.0"),sQuery(id+"F2.wireOp",EDGE,"E12.0.3"),sQuery(id+"F2.wireOp",EDGE,"E12.0.4")])]}),"instanceName":"26"});
            var Q23;
            Q23=makeQuery(id+"F6.opPattern","COPY",EDGE,{"derivedFrom":makeQuery(id+"F3.opLoft","SWEPT_EDGE",EDGE,{"disambiguationData":[OSD([sQuery(id+"F0.wireOp",EDGE,"E0"),sQuery(id+"F0.wireOp",EDGE,"E2"),sQuery(id+"F2.wireOp",EDGE,"E11.0.0"),sQuery(id+"F2.wireOp",EDGE,"E12.0.3"),sQuery(id+"F2.wireOp",EDGE,"E12.0.4")])]}),"instanceName":"25"});
            var Q24;
            Q24=makeQuery(id+"F6.opPattern","COPY",EDGE,{"derivedFrom":makeQuery(id+"F3.opLoft","SWEPT_EDGE",EDGE,{"disambiguationData":[OSD([sQuery(id+"F0.wireOp",EDGE,"E0"),sQuery(id+"F0.wireOp",EDGE,"E2"),sQuery(id+"F2.wireOp",EDGE,"E11.0.0"),sQuery(id+"F2.wireOp",EDGE,"E12.0.3"),sQuery(id+"F2.wireOp",EDGE,"E12.0.4")])]}),"instanceName":"24"});
            var Q25;
            Q25=makeQuery(id+"F6.opPattern","COPY",EDGE,{"derivedFrom":makeQuery(id+"F3.opLoft","SWEPT_EDGE",EDGE,{"disambiguationData":[OSD([sQuery(id+"F0.wireOp",EDGE,"E0"),sQuery(id+"F0.wireOp",EDGE,"E2"),sQuery(id+"F2.wireOp",EDGE,"E11.0.0"),sQuery(id+"F2.wireOp",EDGE,"E12.0.3"),sQuery(id+"F2.wireOp",EDGE,"E12.0.4")])]}),"instanceName":"23"});
            var Q26;
            Q26=makeQuery(id+"F6.opPattern","COPY",EDGE,{"derivedFrom":makeQuery(id+"F3.opLoft","SWEPT_EDGE",EDGE,{"disambiguationData":[OSD([sQuery(id+"F0.wireOp",EDGE,"E0"),sQuery(id+"F0.wireOp",EDGE,"E2"),sQuery(id+"F2.wireOp",EDGE,"E11.0.0"),sQuery(id+"F2.wireOp",EDGE,"E12.0.3"),sQuery(id+"F2.wireOp",EDGE,"E12.0.4")])]}),"instanceName":"22"});
            var Q27;
            Q27=makeQuery(id+"F6.opPattern","COPY",EDGE,{"derivedFrom":makeQuery(id+"F3.opLoft","SWEPT_EDGE",EDGE,{"disambiguationData":[OSD([sQuery(id+"F0.wireOp",EDGE,"E0"),sQuery(id+"F0.wireOp",EDGE,"E2"),sQuery(id+"F2.wireOp",EDGE,"E11.0.0"),sQuery(id+"F2.wireOp",EDGE,"E12.0.3"),sQuery(id+"F2.wireOp",EDGE,"E12.0.4")])]}),"instanceName":"21"});
            var Q28;
            Q28=makeQuery(id+"F6.opPattern","COPY",EDGE,{"derivedFrom":makeQuery(id+"F3.opLoft","SWEPT_EDGE",EDGE,{"disambiguationData":[OSD([sQuery(id+"F0.wireOp",EDGE,"E0"),sQuery(id+"F0.wireOp",EDGE,"E2"),sQuery(id+"F2.wireOp",EDGE,"E11.0.0"),sQuery(id+"F2.wireOp",EDGE,"E12.0.3"),sQuery(id+"F2.wireOp",EDGE,"E12.0.4")])]}),"instanceName":"20"});
            var Q29;
            Q29=makeQuery(id+"F6.opPattern","COPY",EDGE,{"derivedFrom":makeQuery(id+"F3.opLoft","SWEPT_EDGE",EDGE,{"disambiguationData":[OSD([sQuery(id+"F0.wireOp",EDGE,"E0"),sQuery(id+"F0.wireOp",EDGE,"E2"),sQuery(id+"F2.wireOp",EDGE,"E11.0.0"),sQuery(id+"F2.wireOp",EDGE,"E12.0.3"),sQuery(id+"F2.wireOp",EDGE,"E12.0.4")])]}),"instanceName":"19"});
            var Q30;
            Q30=makeQuery(id+"F6.opPattern","COPY",EDGE,{"derivedFrom":makeQuery(id+"F3.opLoft","SWEPT_EDGE",EDGE,{"disambiguationData":[OSD([sQuery(id+"F0.wireOp",EDGE,"E0"),sQuery(id+"F0.wireOp",EDGE,"E2"),sQuery(id+"F2.wireOp",EDGE,"E11.0.0"),sQuery(id+"F2.wireOp",EDGE,"E12.0.3"),sQuery(id+"F2.wireOp",EDGE,"E12.0.4")])]}),"instanceName":"18"});
            var Q31;
            Q31=makeQuery(id+"F6.opPattern","COPY",EDGE,{"derivedFrom":makeQuery(id+"F3.opLoft","SWEPT_EDGE",EDGE,{"disambiguationData":[OSD([sQuery(id+"F0.wireOp",EDGE,"E0"),sQuery(id+"F0.wireOp",EDGE,"E2"),sQuery(id+"F2.wireOp",EDGE,"E11.0.0"),sQuery(id+"F2.wireOp",EDGE,"E12.0.3"),sQuery(id+"F2.wireOp",EDGE,"E12.0.4")])]}),"instanceName":"17"});
            var Q32;
            Q32=makeQuery(id+"F6.opPattern","COPY",EDGE,{"derivedFrom":makeQuery(id+"F3.opLoft","SWEPT_EDGE",EDGE,{"disambiguationData":[OSD([sQuery(id+"F0.wireOp",EDGE,"E0"),sQuery(id+"F0.wireOp",EDGE,"E2"),sQuery(id+"F2.wireOp",EDGE,"E11.0.0"),sQuery(id+"F2.wireOp",EDGE,"E12.0.3"),sQuery(id+"F2.wireOp",EDGE,"E12.0.4")])]}),"instanceName":"16"});
            var Q33;
            Q33=makeQuery(id+"F6.opPattern","COPY",EDGE,{"derivedFrom":makeQuery(id+"F3.opLoft","SWEPT_EDGE",EDGE,{"disambiguationData":[OSD([sQuery(id+"F0.wireOp",EDGE,"E0"),sQuery(id+"F0.wireOp",EDGE,"E2"),sQuery(id+"F2.wireOp",EDGE,"E11.0.0"),sQuery(id+"F2.wireOp",EDGE,"E12.0.3"),sQuery(id+"F2.wireOp",EDGE,"E12.0.4")])]}),"instanceName":"7"});
            var Q34;
            Q34=makeQuery(id+"F6.opPattern","COPY",EDGE,{"derivedFrom":makeQuery(id+"F3.opLoft","SWEPT_EDGE",EDGE,{"disambiguationData":[OSD([sQuery(id+"F0.wireOp",EDGE,"E0"),sQuery(id+"F0.wireOp",EDGE,"E2"),sQuery(id+"F2.wireOp",EDGE,"E11.0.0"),sQuery(id+"F2.wireOp",EDGE,"E12.0.3"),sQuery(id+"F2.wireOp",EDGE,"E12.0.4")])]}),"instanceName":"8"});
            var Q35;
            Q35=makeQuery(id+"F6.opPattern","COPY",EDGE,{"derivedFrom":makeQuery(id+"F3.opLoft","SWEPT_EDGE",EDGE,{"disambiguationData":[OSD([sQuery(id+"F0.wireOp",EDGE,"E0"),sQuery(id+"F0.wireOp",EDGE,"E2"),sQuery(id+"F2.wireOp",EDGE,"E11.0.0"),sQuery(id+"F2.wireOp",EDGE,"E12.0.3"),sQuery(id+"F2.wireOp",EDGE,"E12.0.4")])]}),"instanceName":"9"});
            var Q36;
            Q36=makeQuery(id+"F6.opPattern","COPY",EDGE,{"derivedFrom":makeQuery(id+"F3.opLoft","SWEPT_EDGE",EDGE,{"disambiguationData":[OSD([sQuery(id+"F0.wireOp",EDGE,"E0"),sQuery(id+"F0.wireOp",EDGE,"E2"),sQuery(id+"F2.wireOp",EDGE,"E11.0.0"),sQuery(id+"F2.wireOp",EDGE,"E12.0.3"),sQuery(id+"F2.wireOp",EDGE,"E12.0.4")])]}),"instanceName":"10"});
            var Q37;
            Q37=makeQuery(id+"F6.opPattern","COPY",EDGE,{"derivedFrom":makeQuery(id+"F3.opLoft","SWEPT_EDGE",EDGE,{"disambiguationData":[OSD([sQuery(id+"F0.wireOp",EDGE,"E0"),sQuery(id+"F0.wireOp",EDGE,"E2"),sQuery(id+"F2.wireOp",EDGE,"E11.0.0"),sQuery(id+"F2.wireOp",EDGE,"E12.0.3"),sQuery(id+"F2.wireOp",EDGE,"E12.0.4")])]}),"instanceName":"11"});
            var Q38;
            Q38=makeQuery(id+"F6.opPattern","COPY",EDGE,{"derivedFrom":makeQuery(id+"F3.opLoft","SWEPT_EDGE",EDGE,{"disambiguationData":[OSD([sQuery(id+"F0.wireOp",EDGE,"E0"),sQuery(id+"F0.wireOp",EDGE,"E2"),sQuery(id+"F2.wireOp",EDGE,"E11.0.0"),sQuery(id+"F2.wireOp",EDGE,"E12.0.3"),sQuery(id+"F2.wireOp",EDGE,"E12.0.4")])]}),"instanceName":"12"});
            var Q39;
            Q39=makeQuery(id+"F6.opPattern","COPY",EDGE,{"derivedFrom":makeQuery(id+"F3.opLoft","SWEPT_EDGE",EDGE,{"disambiguationData":[OSD([sQuery(id+"F0.wireOp",EDGE,"E0"),sQuery(id+"F0.wireOp",EDGE,"E2"),sQuery(id+"F2.wireOp",EDGE,"E11.0.0"),sQuery(id+"F2.wireOp",EDGE,"E12.0.3"),sQuery(id+"F2.wireOp",EDGE,"E12.0.4")])]}),"instanceName":"13"});
            var Q40;
            Q40=makeQuery(id+"F6.opPattern","COPY",EDGE,{"derivedFrom":makeQuery(id+"F3.opLoft","SWEPT_EDGE",EDGE,{"disambiguationData":[OSD([sQuery(id+"F0.wireOp",EDGE,"E0"),sQuery(id+"F0.wireOp",EDGE,"E2"),sQuery(id+"F2.wireOp",EDGE,"E11.0.0"),sQuery(id+"F2.wireOp",EDGE,"E12.0.3"),sQuery(id+"F2.wireOp",EDGE,"E12.0.4")])]}),"instanceName":"14"});
            var Q41;
            Q41=makeQuery(id+"F6.opPattern","COPY",EDGE,{"derivedFrom":makeQuery(id+"F3.opLoft","SWEPT_EDGE",EDGE,{"disambiguationData":[OSD([sQuery(id+"F0.wireOp",EDGE,"E0"),sQuery(id+"F0.wireOp",EDGE,"E2"),sQuery(id+"F2.wireOp",EDGE,"E11.0.0"),sQuery(id+"F2.wireOp",EDGE,"E12.0.3"),sQuery(id+"F2.wireOp",EDGE,"E12.0.4")])]}),"instanceName":"15"});
            var Q42;
            Q42=makeQuery(id+"F6.opPattern","COPY",EDGE,{"derivedFrom":makeQuery(id+"F3.opLoft","SWEPT_EDGE",EDGE,{"disambiguationData":[OSD([sQuery(id+"F0.wireOp",EDGE,"E0"),sQuery(id+"F0.wireOp",EDGE,"E6.MirrorCS"),sQuery(id+"F2.wireOp",EDGE,"E11.0.0"),sQuery(id+"F2.wireOp",EDGE,"E12.0.2"),sQuery(id+"F2.wireOp",EDGE,"E12.0.3")])]}),"instanceName":"18"});
            var Q43;
            Q43=makeQuery(id+"F6.opPattern","COPY",EDGE,{"derivedFrom":makeQuery(id+"F3.opLoft","SWEPT_EDGE",EDGE,{"disambiguationData":[OSD([sQuery(id+"F0.wireOp",EDGE,"E0"),sQuery(id+"F0.wireOp",EDGE,"E6.MirrorCS"),sQuery(id+"F2.wireOp",EDGE,"E11.0.0"),sQuery(id+"F2.wireOp",EDGE,"E12.0.2"),sQuery(id+"F2.wireOp",EDGE,"E12.0.3")])]}),"instanceName":"19"});
            var Q44;
            Q44=makeQuery(id+"F6.opPattern","COPY",EDGE,{"derivedFrom":makeQuery(id+"F3.opLoft","SWEPT_EDGE",EDGE,{"disambiguationData":[OSD([sQuery(id+"F0.wireOp",EDGE,"E0"),sQuery(id+"F0.wireOp",EDGE,"E6.MirrorCS"),sQuery(id+"F2.wireOp",EDGE,"E11.0.0"),sQuery(id+"F2.wireOp",EDGE,"E12.0.2"),sQuery(id+"F2.wireOp",EDGE,"E12.0.3")])]}),"instanceName":"20"});
            var Q45;
            Q45=makeQuery(id+"F6.opPattern","COPY",EDGE,{"derivedFrom":makeQuery(id+"F3.opLoft","SWEPT_EDGE",EDGE,{"disambiguationData":[OSD([sQuery(id+"F0.wireOp",EDGE,"E0"),sQuery(id+"F0.wireOp",EDGE,"E6.MirrorCS"),sQuery(id+"F2.wireOp",EDGE,"E11.0.0"),sQuery(id+"F2.wireOp",EDGE,"E12.0.2"),sQuery(id+"F2.wireOp",EDGE,"E12.0.3")])]}),"instanceName":"21"});
            var Q46;
            Q46=makeQuery(id+"F6.opPattern","COPY",EDGE,{"derivedFrom":makeQuery(id+"F3.opLoft","SWEPT_EDGE",EDGE,{"disambiguationData":[OSD([sQuery(id+"F0.wireOp",EDGE,"E0"),sQuery(id+"F0.wireOp",EDGE,"E6.MirrorCS"),sQuery(id+"F2.wireOp",EDGE,"E11.0.0"),sQuery(id+"F2.wireOp",EDGE,"E12.0.2"),sQuery(id+"F2.wireOp",EDGE,"E12.0.3")])]}),"instanceName":"22"});
            var Q47;
            Q47=makeQuery(id+"F6.opPattern","COPY",EDGE,{"derivedFrom":makeQuery(id+"F3.opLoft","SWEPT_EDGE",EDGE,{"disambiguationData":[OSD([sQuery(id+"F0.wireOp",EDGE,"E0"),sQuery(id+"F0.wireOp",EDGE,"E6.MirrorCS"),sQuery(id+"F2.wireOp",EDGE,"E11.0.0"),sQuery(id+"F2.wireOp",EDGE,"E12.0.2"),sQuery(id+"F2.wireOp",EDGE,"E12.0.3")])]}),"instanceName":"23"});
            var Q48;
            Q48=makeQuery(id+"F6.opPattern","COPY",EDGE,{"derivedFrom":makeQuery(id+"F3.opLoft","SWEPT_EDGE",EDGE,{"disambiguationData":[OSD([sQuery(id+"F0.wireOp",EDGE,"E0"),sQuery(id+"F0.wireOp",EDGE,"E6.MirrorCS"),sQuery(id+"F2.wireOp",EDGE,"E11.0.0"),sQuery(id+"F2.wireOp",EDGE,"E12.0.2"),sQuery(id+"F2.wireOp",EDGE,"E12.0.3")])]}),"instanceName":"24"});
            var Q49;
            Q49=makeQuery(id+"F6.opPattern","COPY",EDGE,{"derivedFrom":makeQuery(id+"F3.opLoft","SWEPT_EDGE",EDGE,{"disambiguationData":[OSD([sQuery(id+"F0.wireOp",EDGE,"E0"),sQuery(id+"F0.wireOp",EDGE,"E6.MirrorCS"),sQuery(id+"F2.wireOp",EDGE,"E11.0.0"),sQuery(id+"F2.wireOp",EDGE,"E12.0.2"),sQuery(id+"F2.wireOp",EDGE,"E12.0.3")])]}),"instanceName":"25"});
            var Q50;
            Q50=makeQuery(id+"F6.opPattern","COPY",EDGE,{"derivedFrom":makeQuery(id+"F3.opLoft","SWEPT_EDGE",EDGE,{"disambiguationData":[OSD([sQuery(id+"F0.wireOp",EDGE,"E0"),sQuery(id+"F0.wireOp",EDGE,"E6.MirrorCS"),sQuery(id+"F2.wireOp",EDGE,"E11.0.0"),sQuery(id+"F2.wireOp",EDGE,"E12.0.2"),sQuery(id+"F2.wireOp",EDGE,"E12.0.3")])]}),"instanceName":"27"});
            var Q51;
            Q51=makeQuery(id+"F6.opPattern","COPY",EDGE,{"derivedFrom":makeQuery(id+"F3.opLoft","SWEPT_EDGE",EDGE,{"disambiguationData":[OSD([sQuery(id+"F0.wireOp",EDGE,"E0"),sQuery(id+"F0.wireOp",EDGE,"E6.MirrorCS"),sQuery(id+"F2.wireOp",EDGE,"E11.0.0"),sQuery(id+"F2.wireOp",EDGE,"E12.0.2"),sQuery(id+"F2.wireOp",EDGE,"E12.0.3")])]}),"instanceName":"28"});
            var Q52;
            Q52=makeQuery(id+"F6.opPattern","COPY",EDGE,{"derivedFrom":makeQuery(id+"F3.opLoft","SWEPT_EDGE",EDGE,{"disambiguationData":[OSD([sQuery(id+"F0.wireOp",EDGE,"E0"),sQuery(id+"F0.wireOp",EDGE,"E6.MirrorCS"),sQuery(id+"F2.wireOp",EDGE,"E11.0.0"),sQuery(id+"F2.wireOp",EDGE,"E12.0.2"),sQuery(id+"F2.wireOp",EDGE,"E12.0.3")])]}),"instanceName":"29"});
            var Q53;
            Q53=makeQuery(id+"F6.opPattern","COPY",EDGE,{"derivedFrom":makeQuery(id+"F3.opLoft","SWEPT_EDGE",EDGE,{"disambiguationData":[OSD([sQuery(id+"F0.wireOp",EDGE,"E0"),sQuery(id+"F0.wireOp",EDGE,"E2"),sQuery(id+"F2.wireOp",EDGE,"E11.0.0"),sQuery(id+"F2.wireOp",EDGE,"E12.0.3"),sQuery(id+"F2.wireOp",EDGE,"E12.0.4")])]}),"instanceName":"1"});
            var Q54;
            Q54=makeQuery(id+"F6.opPattern","COPY",EDGE,{"derivedFrom":makeQuery(id+"F3.opLoft","SWEPT_EDGE",EDGE,{"disambiguationData":[OSD([sQuery(id+"F0.wireOp",EDGE,"E0"),sQuery(id+"F0.wireOp",EDGE,"E2"),sQuery(id+"F2.wireOp",EDGE,"E11.0.0"),sQuery(id+"F2.wireOp",EDGE,"E12.0.3"),sQuery(id+"F2.wireOp",EDGE,"E12.0.4")])]}),"instanceName":"2"});
            var Q55;
            Q55=makeQuery(id+"F6.opPattern","COPY",EDGE,{"derivedFrom":makeQuery(id+"F3.opLoft","SWEPT_EDGE",EDGE,{"disambiguationData":[OSD([sQuery(id+"F0.wireOp",EDGE,"E0"),sQuery(id+"F0.wireOp",EDGE,"E2"),sQuery(id+"F2.wireOp",EDGE,"E11.0.0"),sQuery(id+"F2.wireOp",EDGE,"E12.0.3"),sQuery(id+"F2.wireOp",EDGE,"E12.0.4")])]}),"instanceName":"3"});
            var Q56;
            Q56=makeQuery(id+"F6.opPattern","COPY",EDGE,{"derivedFrom":makeQuery(id+"F3.opLoft","SWEPT_EDGE",EDGE,{"disambiguationData":[OSD([sQuery(id+"F0.wireOp",EDGE,"E0"),sQuery(id+"F0.wireOp",EDGE,"E2"),sQuery(id+"F2.wireOp",EDGE,"E11.0.0"),sQuery(id+"F2.wireOp",EDGE,"E12.0.3"),sQuery(id+"F2.wireOp",EDGE,"E12.0.4")])]}),"instanceName":"4"});
            var Q57;
            Q57=makeQuery(id+"F6.opPattern","COPY",EDGE,{"derivedFrom":makeQuery(id+"F3.opLoft","SWEPT_EDGE",EDGE,{"disambiguationData":[OSD([sQuery(id+"F0.wireOp",EDGE,"E0"),sQuery(id+"F0.wireOp",EDGE,"E2"),sQuery(id+"F2.wireOp",EDGE,"E11.0.0"),sQuery(id+"F2.wireOp",EDGE,"E12.0.3"),sQuery(id+"F2.wireOp",EDGE,"E12.0.4")])]}),"instanceName":"5"});
            var Q58;
            Q58=makeQuery(id+"F6.opPattern","COPY",EDGE,{"derivedFrom":makeQuery(id+"F3.opLoft","SWEPT_EDGE",EDGE,{"disambiguationData":[OSD([sQuery(id+"F0.wireOp",EDGE,"E0"),sQuery(id+"F0.wireOp",EDGE,"E2"),sQuery(id+"F2.wireOp",EDGE,"E11.0.0"),sQuery(id+"F2.wireOp",EDGE,"E12.0.3"),sQuery(id+"F2.wireOp",EDGE,"E12.0.4")])]}),"instanceName":"6"});
            var Q59;
            Q59=makeQuery(id+"F6.opPattern","COPY",EDGE,{"derivedFrom":makeQuery(id+"F3.opLoft","SWEPT_EDGE",EDGE,{"disambiguationData":[OSD([sQuery(id+"F0.wireOp",EDGE,"E0"),sQuery(id+"F0.wireOp",EDGE,"E6.MirrorCS"),sQuery(id+"F2.wireOp",EDGE,"E11.0.0"),sQuery(id+"F2.wireOp",EDGE,"E12.0.2"),sQuery(id+"F2.wireOp",EDGE,"E12.0.3")])]}),"instanceName":"8"});
            var Q60;
            Q60=makeQuery(id+"F6.opPattern","COPY",EDGE,{"derivedFrom":makeQuery(id+"F3.opLoft","SWEPT_EDGE",EDGE,{"disambiguationData":[OSD([sQuery(id+"F0.wireOp",EDGE,"E0"),sQuery(id+"F0.wireOp",EDGE,"E6.MirrorCS"),sQuery(id+"F2.wireOp",EDGE,"E11.0.0"),sQuery(id+"F2.wireOp",EDGE,"E12.0.2"),sQuery(id+"F2.wireOp",EDGE,"E12.0.3")])]}),"instanceName":"26"});
            var Q61;
            Q61=makeQuery(id+"F6.opPattern","COPY",EDGE,{"derivedFrom":makeQuery(id+"F3.opLoft","SWEPT_EDGE",EDGE,{"disambiguationData":[OSD([sQuery(id+"F0.wireOp",EDGE,"E0"),sQuery(id+"F0.wireOp",EDGE,"E6.MirrorCS"),sQuery(id+"F2.wireOp",EDGE,"E11.0.0"),sQuery(id+"F2.wireOp",EDGE,"E12.0.2"),sQuery(id+"F2.wireOp",EDGE,"E12.0.3")])]}),"instanceName":"17"});
            var Q62;
            Q62=makeQuery(id+"F6.opPattern","COPY",EDGE,{"derivedFrom":makeQuery(id+"F3.opLoft","SWEPT_EDGE",EDGE,{"disambiguationData":[OSD([sQuery(id+"F0.wireOp",EDGE,"E0"),sQuery(id+"F0.wireOp",EDGE,"E6.MirrorCS"),sQuery(id+"F2.wireOp",EDGE,"E11.0.0"),sQuery(id+"F2.wireOp",EDGE,"E12.0.2"),sQuery(id+"F2.wireOp",EDGE,"E12.0.3")])]}),"instanceName":"16"});
            var Q63;
            Q63=makeQuery(id+"F6.opPattern","COPY",EDGE,{"derivedFrom":makeQuery(id+"F3.opLoft","SWEPT_EDGE",EDGE,{"disambiguationData":[OSD([sQuery(id+"F0.wireOp",EDGE,"E0"),sQuery(id+"F0.wireOp",EDGE,"E6.MirrorCS"),sQuery(id+"F2.wireOp",EDGE,"E11.0.0"),sQuery(id+"F2.wireOp",EDGE,"E12.0.2"),sQuery(id+"F2.wireOp",EDGE,"E12.0.3")])]}),"instanceName":"15"});
            var Q64;
            Q64=makeQuery(id+"F6.opPattern","COPY",EDGE,{"derivedFrom":makeQuery(id+"F3.opLoft","SWEPT_EDGE",EDGE,{"disambiguationData":[OSD([sQuery(id+"F0.wireOp",EDGE,"E0"),sQuery(id+"F0.wireOp",EDGE,"E6.MirrorCS"),sQuery(id+"F2.wireOp",EDGE,"E11.0.0"),sQuery(id+"F2.wireOp",EDGE,"E12.0.2"),sQuery(id+"F2.wireOp",EDGE,"E12.0.3")])]}),"instanceName":"14"});
            var Q65;
            Q65=makeQuery(id+"F6.opPattern","COPY",EDGE,{"derivedFrom":makeQuery(id+"F3.opLoft","SWEPT_EDGE",EDGE,{"disambiguationData":[OSD([sQuery(id+"F0.wireOp",EDGE,"E0"),sQuery(id+"F0.wireOp",EDGE,"E6.MirrorCS"),sQuery(id+"F2.wireOp",EDGE,"E11.0.0"),sQuery(id+"F2.wireOp",EDGE,"E12.0.2"),sQuery(id+"F2.wireOp",EDGE,"E12.0.3")])]}),"instanceName":"13"});
            var Q66;
            Q66=makeQuery(id+"F6.opPattern","COPY",EDGE,{"derivedFrom":makeQuery(id+"F3.opLoft","SWEPT_EDGE",EDGE,{"disambiguationData":[OSD([sQuery(id+"F0.wireOp",EDGE,"E0"),sQuery(id+"F0.wireOp",EDGE,"E6.MirrorCS"),sQuery(id+"F2.wireOp",EDGE,"E11.0.0"),sQuery(id+"F2.wireOp",EDGE,"E12.0.2"),sQuery(id+"F2.wireOp",EDGE,"E12.0.3")])]}),"instanceName":"12"});
            var Q67;
            Q67=makeQuery(id+"F6.opPattern","COPY",EDGE,{"derivedFrom":makeQuery(id+"F3.opLoft","SWEPT_EDGE",EDGE,{"disambiguationData":[OSD([sQuery(id+"F0.wireOp",EDGE,"E0"),sQuery(id+"F0.wireOp",EDGE,"E6.MirrorCS"),sQuery(id+"F2.wireOp",EDGE,"E11.0.0"),sQuery(id+"F2.wireOp",EDGE,"E12.0.2"),sQuery(id+"F2.wireOp",EDGE,"E12.0.3")])]}),"instanceName":"11"});
            var Q68;
            Q68=makeQuery(id+"F6.opPattern","COPY",EDGE,{"derivedFrom":makeQuery(id+"F3.opLoft","SWEPT_EDGE",EDGE,{"disambiguationData":[OSD([sQuery(id+"F0.wireOp",EDGE,"E0"),sQuery(id+"F0.wireOp",EDGE,"E6.MirrorCS"),sQuery(id+"F2.wireOp",EDGE,"E11.0.0"),sQuery(id+"F2.wireOp",EDGE,"E12.0.2"),sQuery(id+"F2.wireOp",EDGE,"E12.0.3")])]}),"instanceName":"10"});
            var Q69;
            Q69=makeQuery(id+"F6.opPattern","COPY",EDGE,{"derivedFrom":makeQuery(id+"F3.opLoft","SWEPT_EDGE",EDGE,{"disambiguationData":[OSD([sQuery(id+"F0.wireOp",EDGE,"E0"),sQuery(id+"F0.wireOp",EDGE,"E6.MirrorCS"),sQuery(id+"F2.wireOp",EDGE,"E11.0.0"),sQuery(id+"F2.wireOp",EDGE,"E12.0.2"),sQuery(id+"F2.wireOp",EDGE,"E12.0.3")])]}),"instanceName":"9"});
            fillet(context, id + "F8", {"entities" : qUnion([Q0, Q1, Q2, Q3, Q4, Q5, Q6, Q7, Q8, Q9, Q10, Q11, Q12, Q13, Q14, Q15, Q16, Q17, Q18, Q19, Q20, Q21, Q22, Q23, Q24, Q25, Q26, Q27, Q28, Q29, Q30, Q31, Q32, Q33, Q34, Q35, Q36, Q37, Q38, Q39, Q40, Q41, Q42, Q43, Q44, Q45, Q46, Q47, Q48, Q49, Q50, Q51, Q52, Q53, Q54, Q55, Q56, Q57, Q58, Q59, Q60, Q61, Q62, Q63, Q64, Q65, Q66, Q67, Q68, Q69]), "radius" : 1.59 * mm, "tangentPropagation" : true, "allowEdgeOverflow" : false});
        }
        {
            var Q0;
            {var subQ3=makeQuery(id+"F3.opLoft","CAP_FACE",FACE,{"disambiguationData":[OSD([makeQuery(id+"F0.imprint","IMPRINT",FACE,{"disambiguationData":[TD([[makeQuery(id+"F0.imprint","IMPRINT",EDGE,{"derivedFrom":sQuery(id+"F0.wireOp",EDGE,"E1.trimOffspring")}),1.0]])]})])],"isStart":true});Q0=makeQuery(id+"F7.opBoolean","MERGE",FACE,{"derivedFrom":[subQ3,makeQuery(id+"F5.opExtrude","CAP_FACE",FACE,{"disambiguationData":[OSD([sQuery(id+"F4.wireOp",EDGE,"E13")])],"isStart":true}),makeQuery(id+"F6.opPattern","COPY",FACE,{"derivedFrom":subQ3,"instanceName":"1"}),makeQuery(id+"F6.opPattern","COPY",FACE,{"derivedFrom":subQ3,"instanceName":"2"}),makeQuery(id+"F6.opPattern","COPY",FACE,{"derivedFrom":subQ3,"instanceName":"3"}),makeQuery(id+"F6.opPattern","COPY",FACE,{"derivedFrom":subQ3,"instanceName":"4"}),makeQuery(id+"F6.opPattern","COPY",FACE,{"derivedFrom":subQ3,"instanceName":"5"}),makeQuery(id+"F6.opPattern","COPY",FACE,{"derivedFrom":subQ3,"instanceName":"6"}),makeQuery(id+"F6.opPattern","COPY",FACE,{"derivedFrom":subQ3,"instanceName":"7"}),makeQuery(id+"F6.opPattern","COPY",FACE,{"derivedFrom":subQ3,"instanceName":"8"}),makeQuery(id+"F6.opPattern","COPY",FACE,{"derivedFrom":subQ3,"instanceName":"9"}),makeQuery(id+"F6.opPattern","COPY",FACE,{"derivedFrom":subQ3,"instanceName":"10"}),makeQuery(id+"F6.opPattern","COPY",FACE,{"derivedFrom":subQ3,"instanceName":"11"}),makeQuery(id+"F6.opPattern","COPY",FACE,{"derivedFrom":subQ3,"instanceName":"12"}),makeQuery(id+"F6.opPattern","COPY",FACE,{"derivedFrom":subQ3,"instanceName":"13"}),makeQuery(id+"F6.opPattern","COPY",FACE,{"derivedFrom":subQ3,"instanceName":"14"}),makeQuery(id+"F6.opPattern","COPY",FACE,{"derivedFrom":subQ3,"instanceName":"15"}),makeQuery(id+"F6.opPattern","COPY",FACE,{"derivedFrom":subQ3,"instanceName":"16"}),makeQuery(id+"F6.opPattern","COPY",FACE,{"derivedFrom":subQ3,"instanceName":"17"}),makeQuery(id+"F6.opPattern","COPY",FACE,{"derivedFrom":subQ3,"instanceName":"18"}),makeQuery(id+"F6.opPattern","COPY",FACE,{"derivedFrom":subQ3,"instanceName":"19"}),makeQuery(id+"F6.opPattern","COPY",FACE,{"derivedFrom":subQ3,"instanceName":"20"}),makeQuery(id+"F6.opPattern","COPY",FACE,{"derivedFrom":subQ3,"instanceName":"21"}),makeQuery(id+"F6.opPattern","COPY",FACE,{"derivedFrom":subQ3,"instanceName":"22"}),makeQuery(id+"F6.opPattern","COPY",FACE,{"derivedFrom":subQ3,"instanceName":"23"}),makeQuery(id+"F6.opPattern","COPY",FACE,{"derivedFrom":subQ3,"instanceName":"24"}),makeQuery(id+"F6.opPattern","COPY",FACE,{"derivedFrom":subQ3,"instanceName":"25"}),makeQuery(id+"F6.opPattern","COPY",FACE,{"derivedFrom":subQ3,"instanceName":"26"}),makeQuery(id+"F6.opPattern","COPY",FACE,{"derivedFrom":subQ3,"instanceName":"27"}),makeQuery(id+"F6.opPattern","COPY",FACE,{"derivedFrom":subQ3,"instanceName":"28"}),makeQuery(id+"F6.opPattern","COPY",FACE,{"derivedFrom":subQ3,"instanceName":"29"}),makeQuery(id+"F6.opPattern","COPY",FACE,{"derivedFrom":subQ3,"instanceName":"30"}),makeQuery(id+"F6.opPattern","COPY",FACE,{"derivedFrom":subQ3,"instanceName":"31"}),makeQuery(id+"F6.opPattern","COPY",FACE,{"derivedFrom":subQ3,"instanceName":"32"}),makeQuery(id+"F6.opPattern","COPY",FACE,{"derivedFrom":subQ3,"instanceName":"33"}),makeQuery(id+"F6.opPattern","COPY",FACE,{"derivedFrom":subQ3,"instanceName":"34"})]});}
            var sketch = newSketch(context, id + "F9", { "sketchPlane" : qUnion([Q0])});
            skCircle(sketch, "E14", {"center": v(0, 0) * mm, "radius": 6.35 * mm});
            skSolve(sketch);
        }
        {
            var Q0;
            Q0 = qSketchRegion(id + "F9", true);
            extrude(context, id + "F10", {"entities" : qUnion([Q0]), "operationType" : NewBodyOperationType.REMOVE, "endBound" : BoundingType.THROUGH_ALL, "oppositeDirection" : true, "depth" : 25.4 * mm});
        }
    });
